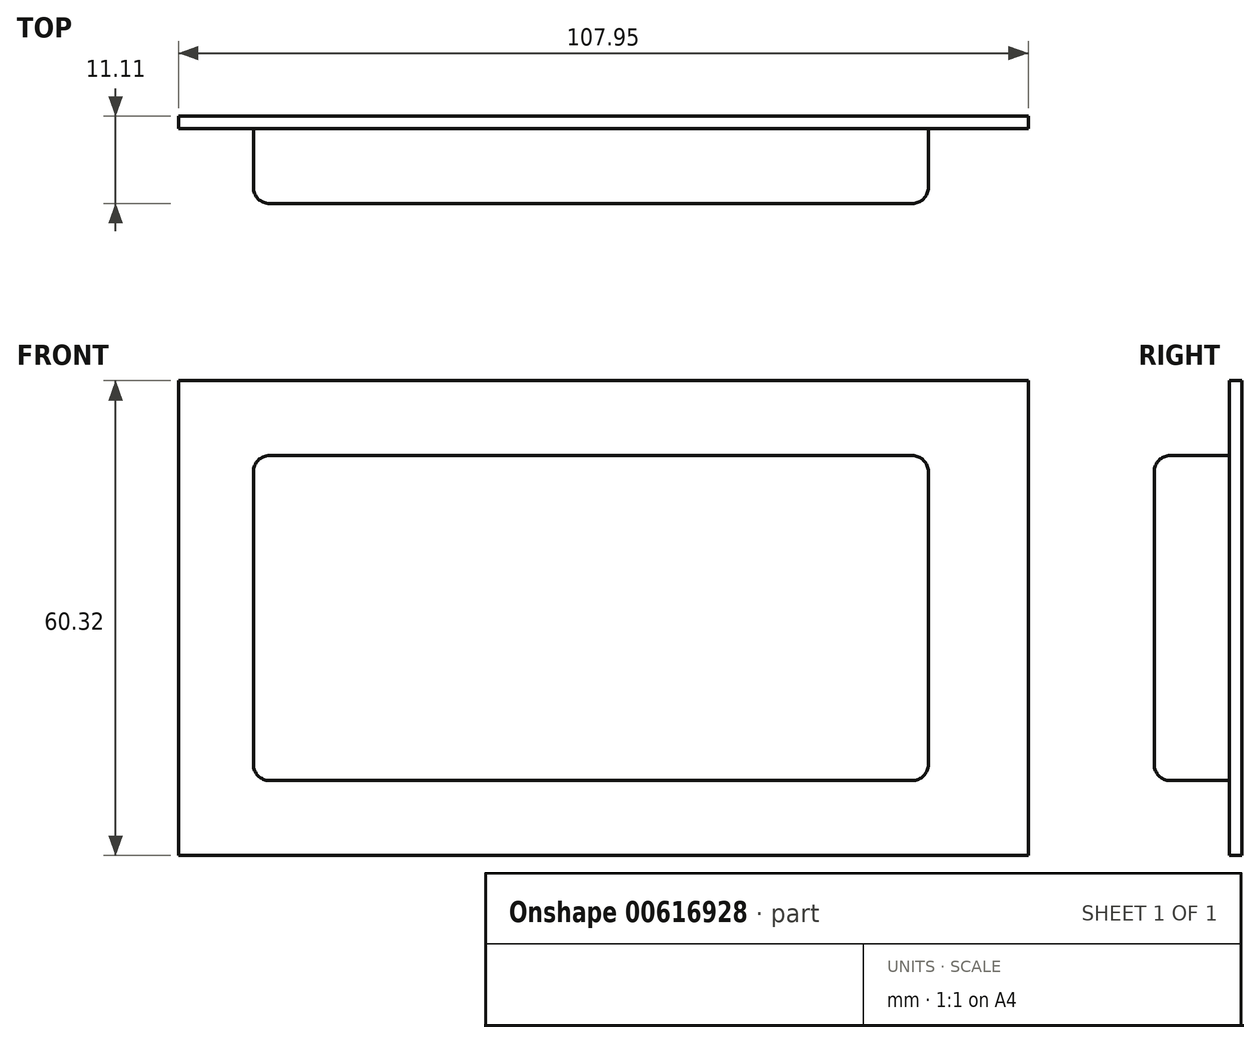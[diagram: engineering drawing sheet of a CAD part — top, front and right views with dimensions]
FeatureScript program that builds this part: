
annotation { "Feature Type Name" : "Feature", "Feature Type Description" : "" }
export const myFeature = defineFeature(function(context is Context, id is Id, definition is map)
    precondition{}
    {
        {
            var Q0;
            Q0=qCreatedBy(makeId("Front.planeOp"),FACE);
            var sketch = newSketch(context, id + "F0", { "sketchPlane" : qUnion([Q0])});
            skLineSegment(sketch, "E0.bottom", {"start": v(-52.39, 30.16) * mm, "end": v(55.56, 30.16) * mm});
            skLineSegment(sketch, "E0.top", {"start": v(-52.39, -30.16) * mm, "end": v(55.56, -30.16) * mm});
            skLineSegment(sketch, "E0.left", {"start": v(-52.39, 30.16) * mm, "end": v(-52.39, -30.16) * mm});
            skLineSegment(sketch, "E0.right", {"start": v(55.56, 30.16) * mm, "end": v(55.56, -30.16) * mm});
            skLineSegment(sketch, "E1.bottom", {"start": v(-42.86, 20.64) * mm, "end": v(42.86, 20.64) * mm});
            skLineSegment(sketch, "E1.top", {"start": v(-42.86, -20.64) * mm, "end": v(42.86, -20.64) * mm});
            skLineSegment(sketch, "E1.left", {"start": v(-42.86, 20.64) * mm, "end": v(-42.86, -20.64) * mm});
            skLineSegment(sketch, "E1.right", {"start": v(42.86, 20.64) * mm, "end": v(42.86, -20.64) * mm});
            skLineSegment(sketch, "E2", {"start": v(-42.86, 20.64) * mm, "end": v(42.86, -20.64) * mm, "construction": true});
            skLineSegment(sketch, "E3", {"start": v(42.86, 20.64) * mm, "end": v(-42.86, -20.64) * mm, "construction": true});
            skPoint(sketch, "E4", {"position": v(0, 0) * mm});
            skSolve(sketch);
        }
        {
            var Q0;
            Q0 = qSketchRegion(id + "F0", true);
            var Q1;
            Q1=makeQuery(id+"F0.imprint","IMPRINT",FACE,{"disambiguationData":[TD([[makeQuery(id+"F0.imprint","IMPRINT",EDGE,{"derivedFrom":sQuery(id+"F0.wireOp",EDGE,"E1.bottom")}),-1.0]])]});
            extrude(context, id + "F1", {"entities" : qUnion([Q0, Q1]), "depth" : 1.59 * mm, "offsetDistance" : 25.4 * mm});
        }
        {
            var Q0;
            Q0=makeQuery(id+"F0.imprint","IMPRINT",FACE,{"disambiguationData":[TD([[makeQuery(id+"F0.imprint","IMPRINT",EDGE,{"derivedFrom":sQuery(id+"F0.wireOp",EDGE,"E1.bottom")}),-1.0]])]});
            extrude(context, id + "F2", {"entities" : qUnion([Q0]), "operationType" : NewBodyOperationType.ADD, "depth" : 11.1 * mm, "offsetDistance" : 25.4 * mm});
        }
        {
            var Q0;
            Q0=makeQuery(id+"F2.opExtrude","SWEPT_EDGE",EDGE,{"disambiguationData":[OSD([sQuery(id+"F0.wireOp",EDGE,"E1.bottom"),sQuery(id+"F0.wireOp",EDGE,"E1.right")])]});
            var Q1;
            Q1=makeQuery(id+"F2.opExtrude","SWEPT_EDGE",EDGE,{"disambiguationData":[OSD([sQuery(id+"F0.wireOp",EDGE,"E1.bottom"),sQuery(id+"F0.wireOp",EDGE,"E1.left")])]});
            var Q2;
            Q2=makeQuery(id+"F2.opExtrude","SWEPT_EDGE",EDGE,{"disambiguationData":[OSD([sQuery(id+"F0.wireOp",EDGE,"E1.top"),sQuery(id+"F0.wireOp",EDGE,"E1.left")])]});
            var Q3;
            Q3=makeQuery(id+"F2.opExtrude","SWEPT_EDGE",EDGE,{"disambiguationData":[OSD([sQuery(id+"F0.wireOp",EDGE,"E1.top"),sQuery(id+"F0.wireOp",EDGE,"E1.right")])]});
            var Q4;
            Q4=makeQuery(id+"F2.opExtrude","CAP_EDGE",EDGE,{"disambiguationData":[OSD([sQuery(id+"F0.wireOp",EDGE,"E1.right")])],"isStart":false});
            var Q5;
            Q5=makeQuery(id+"F2.opExtrude","CAP_EDGE",EDGE,{"disambiguationData":[OSD([sQuery(id+"F0.wireOp",EDGE,"E1.top")])],"isStart":false});
            var Q6;
            Q6=makeQuery(id+"F2.opExtrude","CAP_EDGE",EDGE,{"disambiguationData":[OSD([sQuery(id+"F0.wireOp",EDGE,"E1.left")])],"isStart":false});
            var Q7;
            Q7=makeQuery(id+"F2.opExtrude","CAP_EDGE",EDGE,{"disambiguationData":[OSD([sQuery(id+"F0.wireOp",EDGE,"E1.bottom")])],"isStart":false});
            fillet(context, id + "F3", {"entities" : qUnion([Q0, Q1, Q2, Q3, Q4, Q5, Q6, Q7]), "radius" : 2.03 * mm, "tangentPropagation" : true, "allowEdgeOverflow" : false});
        }
    });
